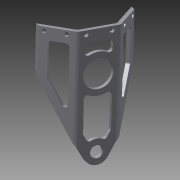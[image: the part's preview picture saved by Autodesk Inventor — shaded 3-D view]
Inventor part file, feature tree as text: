
AUTODESK INVENTOR PART (.ipt)
format: ipt  version: 2012 (Build 160160000, 160)  size: 300,032 bytes
history: native  units: in
note: dims shown in document units (in); Inventor stores cm internally (conversion verified against a paired STEP export)
features: sketch x6, other x4, projected_geometry x4, sheet_metal_op x3, fillet x1
ambient origin geometry x8: Origin, YZ Plane, XZ Plane, XY Plane, X Axis, Y Axis, Z Axis, Center Point
bodies: Solid1 (feature_tree)
feature tree (18):
  sheet_metal_op  "Face1"
  fillet  "Fillet1"  Radius=1.1796in
  sheet_metal_op  "Fold1"
  sheet_metal_op  "Fold2"
  sketch  "Sketch1"  dims[d2=1.289in]
  other  "Plate1"
  sketch  "Sketch3"  dims[d3=0.875in]
  sketch  "Sketch4"  dims[d4=0.5898in]
  sketch  "Sketch5"  dims[d5=3.5in]
  projected_geometry  "Projected Loop1"
  projected_geometry  "Projected Loop2"
  projected_geometry  "Projected Loop3"
  projected_geometry  "Projected Loop4"
  sketch  "Sketch6"  dims[d6=0.375in]
  sketch  "Sketch7"  dims[d7=0.375in d9=0.1875in d10=0.1875in d11=0.625in d12=0.625in d13=0.1875in d14=0.375in d15=0.1875in d16=0.3125in d17=0.3125in d18=0.125in d29=0.375in d30=0.375in d31=0.375in d32=0.375in d33=0.375in d34=0.375in d39=0.0938in d40=0.1875in d41=0.125in d42=0.0625in d43=0.25in d44=0.125in d45=45.0deg d46=0.0625in d47=1.1593in d48=1.1593in d49=0.125in d50=0.0625in d51=0.25in d52=0.125in d53=45.0deg d54=0.0625in d59=1.5in d60=0.0in d61=0.14in d62=0.75in d63=0.2148in d64=0.2148in d65=0.125in d66=0.25in d68=0.625in d69=0.14in d70=0.125in d71=0.125in d72=0.0in d73=0.14in d74=0.125in d75=0.625in d76=0.25in d77=0.125in d78=0.0in d83=0.375in d84=0.25in d85=0.25in]
  other  "Cut2"
  other  "Cut3"
  other  "Cut4"
